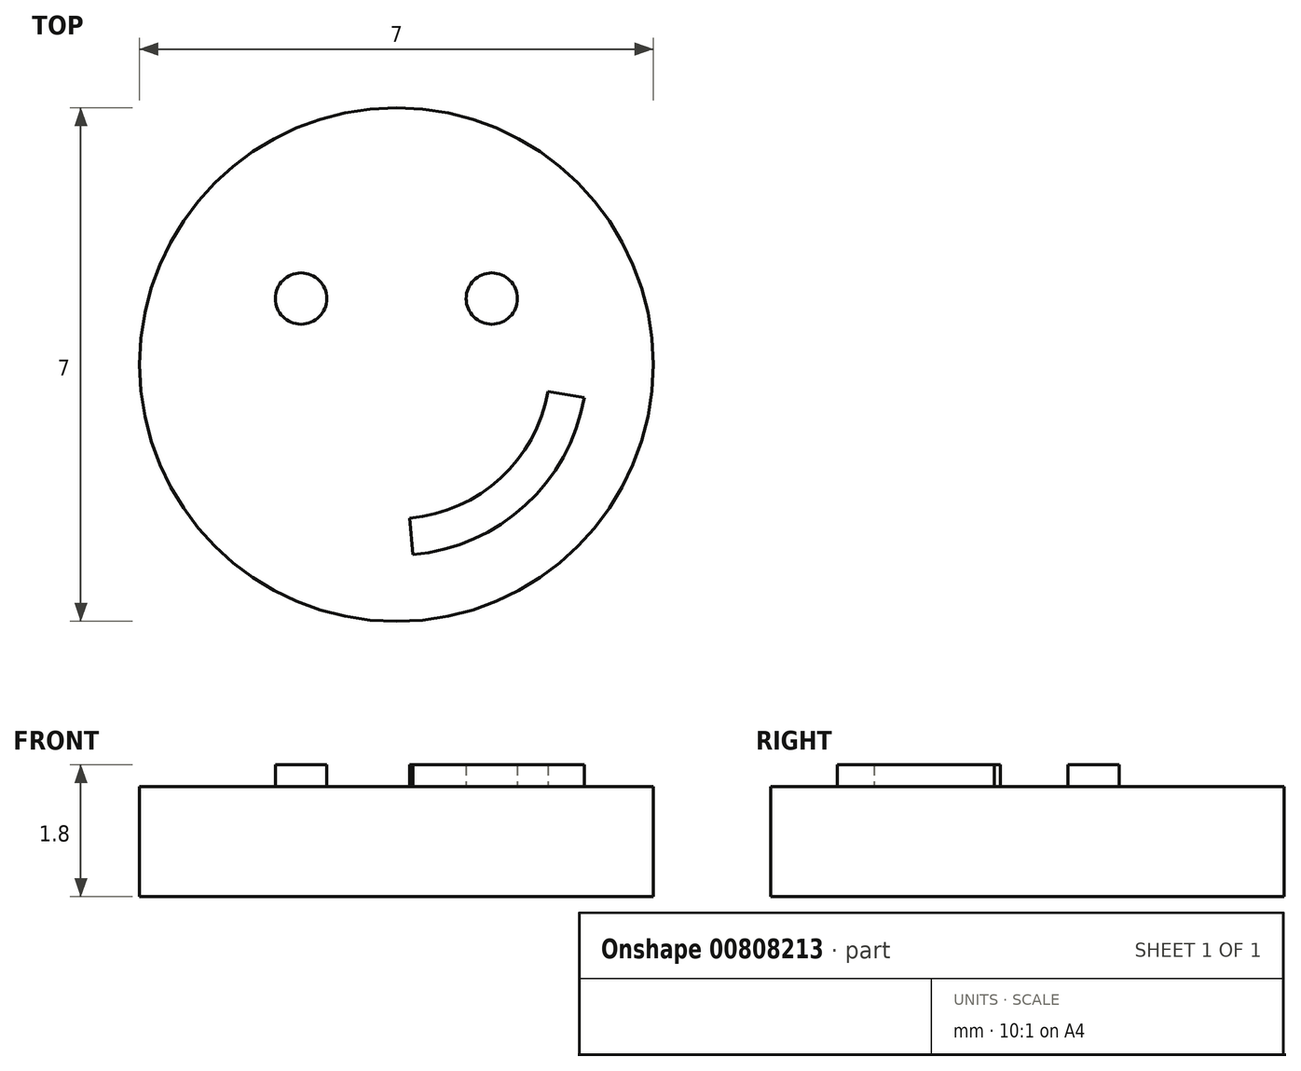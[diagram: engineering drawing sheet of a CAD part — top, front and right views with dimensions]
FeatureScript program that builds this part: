
annotation { "Feature Type Name" : "Feature", "Feature Type Description" : "" }
export const myFeature = defineFeature(function(context is Context, id is Id, definition is map)
    precondition{}
    {
        {
            var Q0;
            Q0=qCreatedBy(makeId("Top.planeOp"),FACE);
            var sketch = newSketch(context, id + "F0", { "sketchPlane" : qUnion([Q0])});
            skCircle(sketch, "E0", {"center": v(0, 0) * mm, "radius": 3.5 * mm});
            skSolve(sketch);
        }
        {
            var Q0;
            Q0=makeQuery(id+"F0.imprint","IMPRINT",FACE,{"disambiguationData":[TD([[makeQuery(id+"F0.imprint","IMPRINT",EDGE,{"derivedFrom":sQuery(id+"F0.wireOp",EDGE,"E0")}),1.0]])]});
            extrude(context, id + "F1", {"entities" : qUnion([Q0]), "depth" : 1.5 * mm, "offsetDistance" : 25 * mm});
        }
        {
            var Q0;
            Q0=qCreatedBy(makeId("Top.planeOp"),FACE);
            var sketch = newSketch(context, id + "F2", { "sketchPlane" : qUnion([Q0])});
            skCircle(sketch, "E1", {"center": v(-1.3, 0.9) * mm, "radius": 0.35 * mm});
            skCircle(sketch, "E2", {"center": v(1.3, 0.9) * mm, "radius": 0.35 * mm});
            skArc(sketch, "E3", {"start": v(0.23, -2.6) * mm, "mid": v(1.76, -1.92) * mm, "end": v(2.56, -0.45) * mm});
            skLineSegment(sketch, "E4", {"start": v(2.07, -0.36) * mm, "end": v(2.56, -0.45) * mm});
            skArc(sketch, "E5.trimOffspring", {"start": v(0.18, -2.1) * mm, "mid": v(1.42, -1.55) * mm, "end": v(2.07, -0.36) * mm});
            skLineSegment(sketch, "E6", {"start": v(0.18, -2.1) * mm, "end": v(0.23, -2.6) * mm});
            skSolve(sketch);
        }
        {
            var Q0;
            Q0 = qSketchRegion(id + "F2", true);
            extrude(context, id + "F3", {"entities" : qUnion([Q0]), "operationType" : NewBodyOperationType.ADD, "depth" : 1.8 * mm, "offsetDistance" : 25 * mm});
        }
    });
